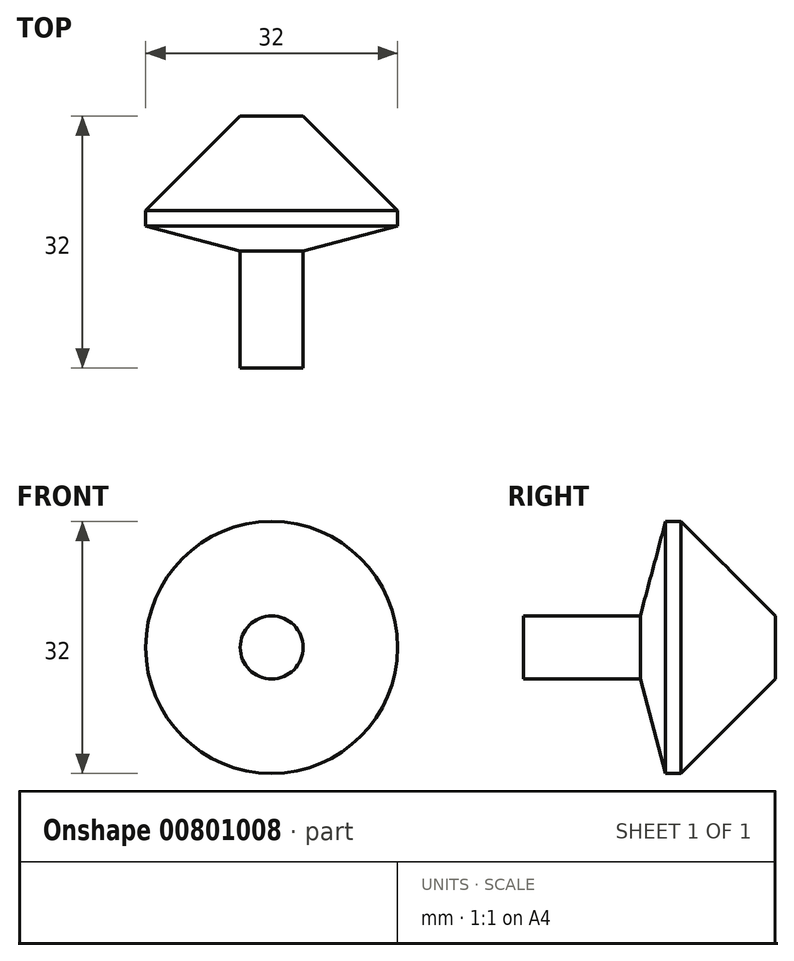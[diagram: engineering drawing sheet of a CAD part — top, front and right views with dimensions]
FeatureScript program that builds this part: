
annotation { "Feature Type Name" : "Feature", "Feature Type Description" : "" }
export const myFeature = defineFeature(function(context is Context, id is Id, definition is map)
    precondition{}
    {
        {
            var Q0;
            Q0=qCreatedBy(makeId("Top.planeOp"),FACE);
            var sketch = newSketch(context, id + "F0", { "sketchPlane" : qUnion([Q0])});
            skLineSegment(sketch, "E0", {"start": v(0, 0) * mm, "end": v(0, -32) * mm});
            skLineSegment(sketch, "E1", {"start": v(0, -32) * mm, "end": v(4, -32) * mm});
            skLineSegment(sketch, "E2", {"start": v(4, -32) * mm, "end": v(4, -22.83) * mm});
            skLineSegment(sketch, "E3", {"start": v(4, 0) * mm, "end": v(0, 0) * mm});
            skLineSegment(sketch, "E4", {"start": v(4, -5.66) * mm, "end": v(4, -13.03) * mm});
            skLineSegment(sketch, "E5", {"start": v(4, -13.03) * mm, "end": v(9.82, -11.47) * mm});
            skLineSegment(sketch, "E6", {"start": v(9.82, -11.47) * mm, "end": v(4, -5.66) * mm});
            skLineSegment(sketch, "E7", {"start": v(4, 0) * mm, "end": v(16, -12) * mm});
            skLineSegment(sketch, "E8", {"start": v(16, -12) * mm, "end": v(16, -13.96) * mm});
            skLineSegment(sketch, "E9", {"start": v(16, -13.96) * mm, "end": v(4, -17.17) * mm});
            skLineSegment(sketch, "E10", {"start": v(4, -17.17) * mm, "end": v(4, -22.83) * mm});
            skSolve(sketch);
        }
        {
            var Q0;
            Q0=makeQuery(id+"F0.imprint","IMPRINT",FACE,{"disambiguationData":[TD([[makeQuery(id+"F0.imprint","IMPRINT",EDGE,{"derivedFrom":sQuery(id+"F0.wireOp",EDGE,"E0")}),1.0]])]});
            var Q1;
            Q1=makeQuery(id+"F0.imprint","IMPRINT",FACE,{"disambiguationData":[TD([[makeQuery(id+"F0.imprint","IMPRINT",EDGE,{"derivedFrom":sQuery(id+"F0.wireOp",EDGE,"E4")}),1.0]])]});
            var Q2;
            Q2=sQuery(id+"F0.wireOp",EDGE,"E0");
            revolve(context, id + "F1", {"surfaceOperationType" : NewSurfaceOperationType.NEW, "entities" : qUnion([Q0, Q1]), "axis" : qUnion([Q2]), "revolveType" : RevolveType.FULL});
        }
    });
